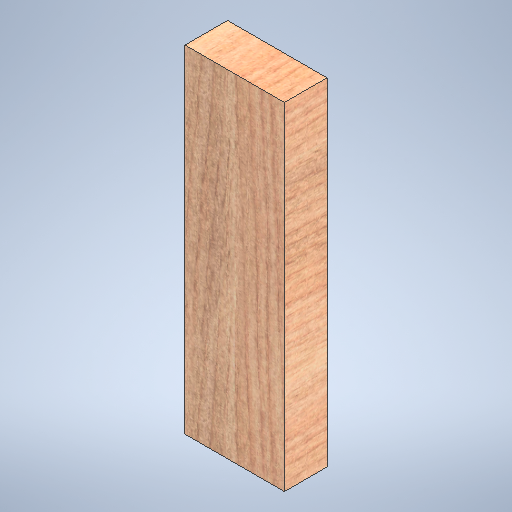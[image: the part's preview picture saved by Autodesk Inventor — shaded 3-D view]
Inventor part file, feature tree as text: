
AUTODESK INVENTOR PART (.ipt)
format: ipt  version: 2025.1 (Build 291241020, 241B)  size: 409,600 bytes
history: native  units: in
note: dims shown in document units (in); Inventor stores cm internally (conversion verified against a paired STEP export)
features: extrude x1, sketch x1
ambient origin geometry x8: Origin, YZ Plane, XZ Plane, XY Plane, X Axis, Y Axis, Z Axis, Center Point
bodies: Solid1 (feature_tree)
feature tree (2):
  extrude  "Extrusion1"  Depth=11.8623in
  sketch  "Sketch1"  dims[d0=3.5in d1=11.8623in d2=1.5in d3=0.0in]
